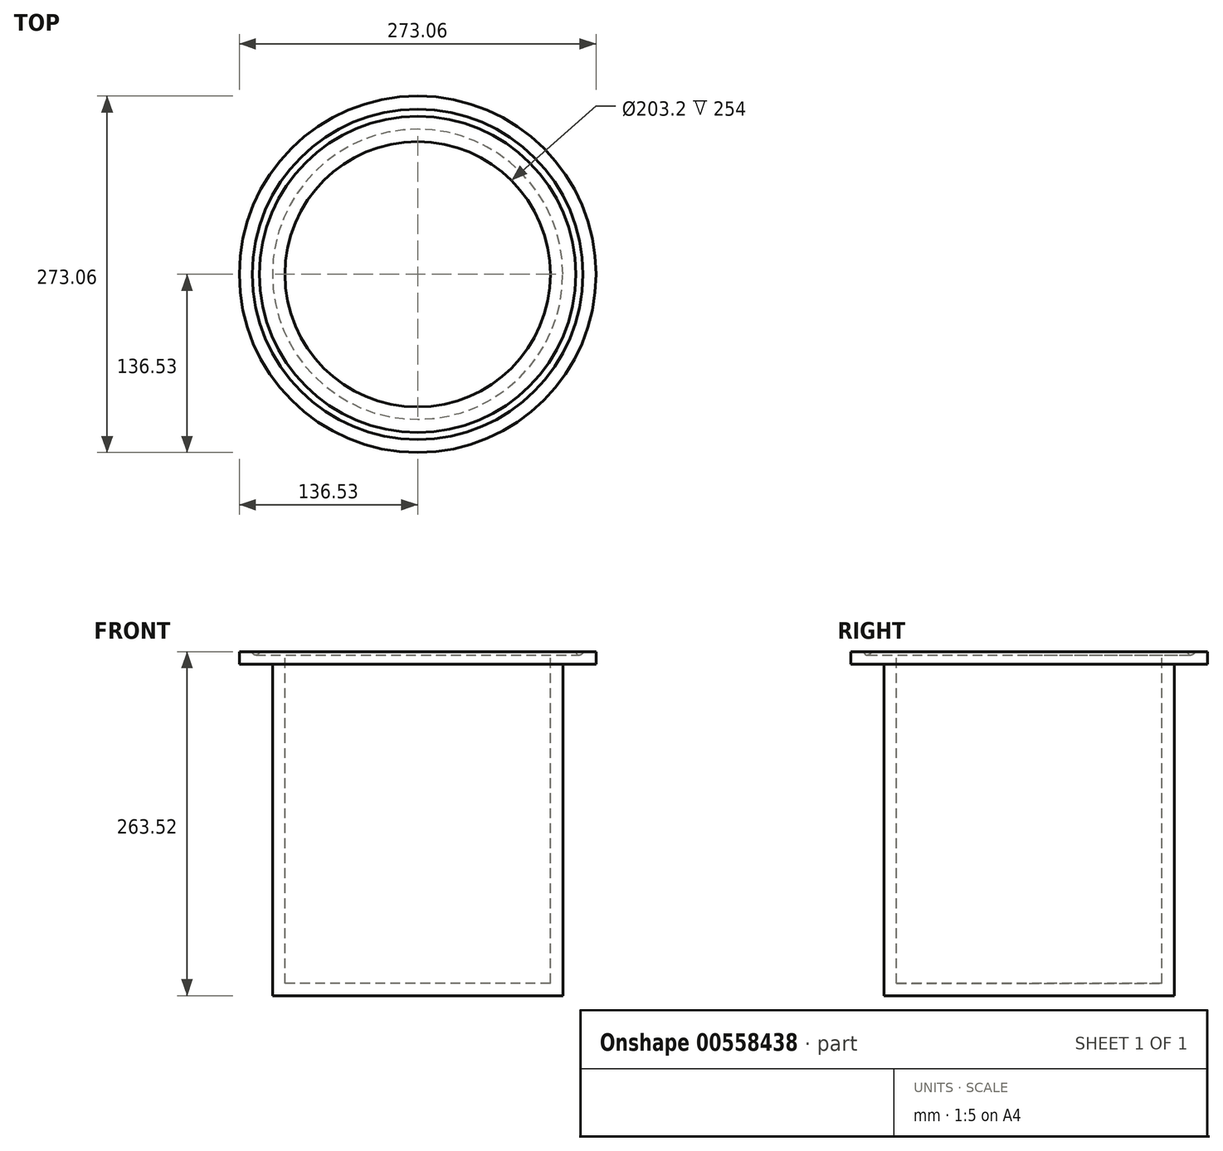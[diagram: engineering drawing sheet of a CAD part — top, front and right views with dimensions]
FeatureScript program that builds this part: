
annotation { "Feature Type Name" : "Feature", "Feature Type Description" : "" }
export const myFeature = defineFeature(function(context is Context, id is Id, definition is map)
    precondition{}
    {
        {
            var Q0;
            Q0=qCreatedBy(makeId("Front.planeOp"),FACE);
            var sketch = newSketch(context, id + "F0", { "sketchPlane" : qUnion([Q0])});
            skLineSegment(sketch, "E0", {"start": v(0, -202.48) * mm, "end": v(0, -212) * mm});
            skLineSegment(sketch, "E1", {"start": v(0, -212) * mm, "end": v(-111.12, -212) * mm});
            skLineSegment(sketch, "E2", {"start": v(-111.12, -212) * mm, "end": v(-111.13, 42) * mm});
            skLineSegment(sketch, "E3", {"start": v(-111.13, 42) * mm, "end": v(-136.53, 42) * mm});
            skLineSegment(sketch, "E4", {"start": v(-136.53, 42) * mm, "end": v(-136.53, 51.52) * mm});
            skLineSegment(sketch, "E5", {"start": v(-136.53, 51.52) * mm, "end": v(-101.6, 51.52) * mm});
            skLineSegment(sketch, "E6", {"start": v(-101.6, 51.52) * mm, "end": v(-101.6, -202.48) * mm});
            skLineSegment(sketch, "E7", {"start": v(-101.6, -202.48) * mm, "end": v(0, -202.48) * mm});
            skLineSegment(sketch, "E8", {"start": v(0, 92.01) * mm, "end": v(0, -249.96) * mm, "construction": true});
            skSolve(sketch);
        }
        {
            var Q0;
            Q0=makeQuery(id+"F0.imprint","IMPRINT",FACE,{"disambiguationData":[TD([[makeQuery(id+"F0.imprint","IMPRINT",EDGE,{"derivedFrom":sQuery(id+"F0.wireOp",EDGE,"E0")}),-1.0]])]});
            var Q1;
            Q1=sQuery(id+"F0.wireOp",EDGE,"E8");
            revolve(context, id + "F1", {"entities" : qUnion([Q0]), "axis" : qUnion([Q1]), "revolveType" : RevolveType.FULL});
        }
        {
            var Q0;
            Q0=makeQuery(id+"F1.opRevolve","SWEPT_FACE",FACE,{"disambiguationData":[OSD([sQuery(id+"F0.wireOp",EDGE,"E5")])]});
            var sketch = newSketch(context, id + "F2", { "sketchPlane" : qUnion([Q0])});
            skCircle(sketch, "E9", {"center": v(0, 0) * mm, "radius": 123.83 * mm});
            skSolve(sketch);
        }
        {
            var Q0;
            Q0=qCreatedBy(makeId("Front.planeOp"),FACE);
            var sketch = newSketch(context, id + "F3", { "sketchPlane" : qUnion([Q0])});
            skArc(sketch, "E10", {"start": v(-126.52, 51.52) * mm, "mid": v(-123.83, 48.83) * mm, "end": v(-121.13, 51.52) * mm});
            skLineSegment(sketch, "E11", {"start": v(-126.52, 51.52) * mm, "end": v(-121.13, 51.52) * mm});
            skSolve(sketch);
        }
        {
            var Q0;
            Q0 = qSketchRegion(id + "F3", true);
            var Q1;
            Q1=sQuery(id+"F2.wireOp",EDGE,"E9");
            sweep(context, id + "F4", {"operationType" : NewBodyOperationType.REMOVE, "profiles" : qUnion([Q0]), "path" : qUnion([Q1])});
        }
    });
